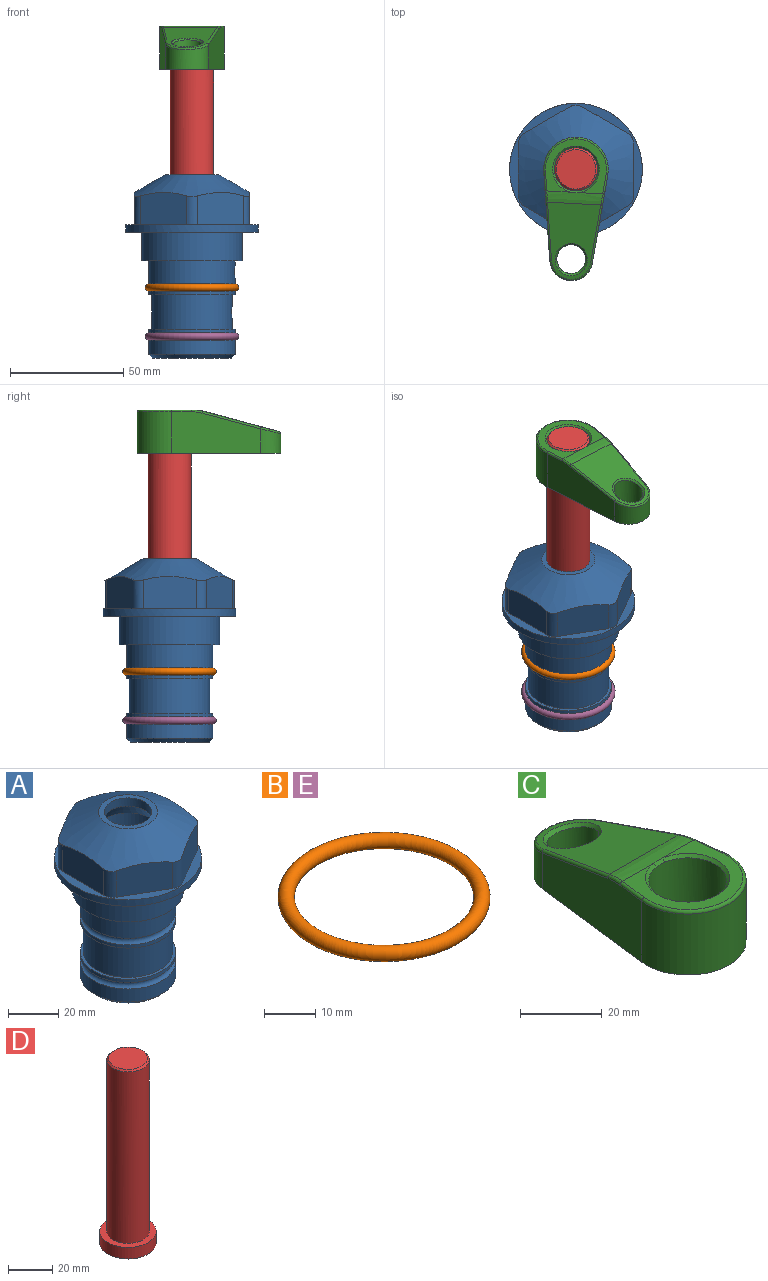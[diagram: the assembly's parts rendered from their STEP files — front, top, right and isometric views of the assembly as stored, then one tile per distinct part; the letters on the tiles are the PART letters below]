
ASSEMBLY  parts=5 mates=4
PART A: 36 faces, bbox 58.7x58.7x81 mm
  f0: cylinder r=17.78mm len=35.56mm, axis (0,0,1), area 1670.8mm2, adj f23,f24,f31
  f1: cylinder r=19.05mm len=38.1mm, axis (0,0,1), area 1191.9mm2, adj f26,f27,f30
  f2: plane 58.66x58.66mm, normal (0,0,-1), area 1150.6mm2, adj f3,f28
  f3: cylinder r=29.33mm len=58.66mm, axis (0,0,-1), area 585.1mm2, adj f2,f4
  f4: plane 58.66x58.66mm, normal (0,0,1), area 475.9mm2, adj f3,f5,f6,f7,f8,f9,f10,f11
  f5: plane 20.32x14.34mm, normal (-0.5,0.87,0), area 324.4mm2, adj f4,f15,f16,f17
  f6: plane 20.32x14.34mm, normal (0.5,0.87,0), area 324.4mm2, adj f4,f14,f15,f17
  f7: plane 23.48x14.34mm, normal (1,0,0), area 324.4mm2, adj f4,f13,f14,f17
  f8: plane 20.32x14.34mm, normal (0.5,-0.87,0), area 324.4mm2, adj f4,f12,f13,f17
  f9: plane 20.32x14.34mm, normal (-0.5,-0.87,0), area 324.4mm2, adj f4,f11,f12,f17
  f10: plane 23.48x14.34mm, normal (-1,0,0), area 324.4mm2, adj f4,f11,f16,f17
  f11: cylinder r=5.08mm len=12.85mm, axis (0,0,-1), area 67.2mm2, adj f4,f9,f10,f17
  f12: cylinder r=5.08mm len=12.85mm, axis (0,0,-1), area 67.2mm2, adj f4,f8,f9,f17
  f13: cylinder r=5.08mm len=12.85mm, axis (0,0,-1), area 67.2mm2, adj f4,f7,f8,f17
  f14: cylinder r=5.08mm len=12.85mm, axis (0,0,-1), area 67.2mm2, adj f4,f6,f7,f17
  f15: cylinder r=5.08mm len=12.85mm, axis (0,0,-1), area 67.2mm2, adj f4,f5,f6,f17
  f16: cylinder r=5.08mm len=12.85mm, axis (0,0,-1), area 67.2mm2, adj f4,f5,f10,f17
  f17: cone r=11.73mm half-angle=60deg, axis (0,0,-1), area 2071.8mm2, adj f5,f6,f7,f8,f9,f10,f11,f12
  f18: plane 23.46x23.46mm, normal (0,0,1), area 147.4mm2, adj f17,f35
  f19: plane 34.93x34.93mm, normal (0,0,-1), area 958mm2, adj f29
  f20: cylinder r=19.05mm len=38.1mm, axis (0,0,1), area 760.1mm2, adj f21,f29
  f21: torus R=19.05mm, axis (0,0,1), area 565.3mm2, adj f20,f22
  f22: cylinder r=19.05mm len=38.1mm, axis (0,0,1), area 190mm2, adj f21,f23
  f23: plane 38.1x38.1mm, normal (0,0,1), area 146.9mm2, adj f0,f22
  f24: plane 38.1x38.1mm, normal (0,0,-1), area 146.9mm2, adj f0,f25
  f25: cylinder r=19.05mm len=38.1mm, axis (0,0,1), area 190mm2, adj f24,f26
  f26: torus R=19.05mm, axis (0,0,1), area 565.3mm2, adj f1,f25
  f27: plane 44.45x44.45mm, normal (0,0,-1), area 411.7mm2, adj f1,f28
  f28: cylinder r=22.23mm len=44.45mm, axis (0,0,1), area 1773.5mm2, adj f2,f27
  f29: cone r=19.05mm half-angle=45deg, axis (0,0,1), area 257.5mm2, adj f19,f20
  f30: cylinder r=3.17mm len=6.75mm, axis (-1,0,0), area 128mm2, adj f1,f33
  f31: cylinder r=3.17mm len=6.35mm, axis (-1,0,0), area 102.5mm2, adj f0,f33
  f32: plane 25.4x25.4mm, normal (0,0,1), area 506.7mm2, adj f33
  f33: cylinder r=12.7mm len=66.42mm, axis (0,0,-1), area 5236.2mm2, adj f30,f31,f32,f34
  f34: cone r=9.53mm half-angle=30deg, axis (0,0,-1), area 443.4mm2, adj f33,f35
  f35: cylinder r=9.53mm len=19.05mm, axis (0,0,-1), area 240.9mm2, adj f18,f34
PART B: 1 faces, bbox 44.7x44.7x3.2 mm
  f0: torus R=19.05mm, axis (0,0,1), area 1193.9mm2
PART C: 31 faces, bbox 31.7x65.5x19.8 mm
  f0: plane 39.12x18.26mm, normal (0.99,0.12,0), area 612.2mm2, adj f1,f4,f7,f11,f13,f15
  f1: cylinder r=9.53mm len=18.91mm, axis (0,0,-1), area 296.1mm2, adj f0,f2,f7,f17
  f2: plane 39.12x18.26mm, normal (-0.99,0.12,0), area 612.2mm2, adj f1,f4,f7,f12,f14,f16
  f3: cylinder r=6.35mm len=12.7mm, axis (0,0,-1), area 362.4mm2, adj f7,f18
  f4: cylinder r=14.29mm len=28.58mm, axis (0,0,-1), area 882.2mm2, adj f0,f2,f7,f10
  f5: cylinder r=9.53mm len=19.05mm, axis (0,0,-1), area 1092.6mm2, adj f7,f19,f20
  f6: plane 26.99x23.69mm, normal (0,0,1), area 216.2mm2, adj f9,f10,f11,f12,f19
  f7: plane 63.5x28.58mm, normal (0,0,-1), area 661.8mm2, adj f0,f1,f2,f3,f4,f5,f22,f23
  f8: plane 33.52x23.6mm, normal (0,0.26,0.97), area 486mm2, adj f9,f15,f16,f17,f18
  f9: cylinder r=19.05mm len=24.72mm, axis (1,0,0), area 120.4mm2, adj f6,f8,f13,f14,f20
  f10: torus R=13.49mm, axis (0,0,1), area 59mm2, adj f4,f6,f11,f12
  f11: cylinder r=0.79mm len=8.67mm, axis (0.12,-0.99,0), area 10.8mm2, adj f0,f6,f10,f13
  f12: cylinder r=0.79mm len=8.67mm, axis (0.12,0.99,0), area 10.8mm2, adj f2,f6,f10,f14
  f13: bspline ~4.95x1.42mm, area 6.1mm2, adj f0,f9,f11,f15
  f14: bspline ~4.95x1.42mm, area 6.1mm2, adj f2,f9,f12,f16
  f15: cylinder r=0.79mm len=25.95mm, axis (0.12,-0.96,0.26), area 32.9mm2, adj f0,f8,f13,f17
  f16: cylinder r=0.79mm len=25.95mm, axis (0.12,0.96,-0.26), area 32.9mm2, adj f2,f8,f14,f17
  f17: bspline ~18.91x8.38mm, area 30mm2, adj f1,f8,f15,f16
  f18: bspline ~14.29x14.29mm, area 48.3mm2, adj f3,f8
  f19: cone r=9.53mm half-angle=45deg, axis (0,0,1), area 66.5mm2, adj f5,f6,f20
  f20: bspline ~3.22x0.96mm, area 3.5mm2, adj f5,f9,f19
  f21: plane 2.75x2.72mm, normal (0,0,-1), area 2.9mm2, adj f23,f25,f28
  f22: plane 23.05x15.88mm, normal (-0.99,-0.12,0), area 323.6mm2, adj f7,f25,f26,f27,f28,f29
  f23: plane 23.05x15.88mm, normal (0.99,-0.12,0), area 323.6mm2, adj f7,f21,f25,f27,f28,f30
  f24: cylinder r=9.53mm len=10.69mm, axis (0,0,-1), area 114.7mm2, adj f7,f27,f29,f30
  f25: cylinder r=12.7mm len=20.59mm, axis (0,0,-1), area 381.1mm2, adj f7,f21,f22,f23,f26,f28
  f26: plane 2.75x2.72mm, normal (0,0,-1), area 2.9mm2, adj f22,f25,f28
  f27: plane 19.72x18.37mm, normal (0,-0.26,-0.97), area 291.8mm2, adj f22,f23,f24,f28,f29,f30
  f28: cylinder r=15.88mm len=19.92mm, axis (1,0,0), area 54.8mm2, adj f21,f22,f23,f25,f26,f27
  f29: cylinder r=1.59mm len=11mm, axis (0,0,-1), area 34.7mm2, adj f7,f22,f24,f27
  f30: cylinder r=1.59mm len=11mm, axis (0,0,-1), area 34.7mm2, adj f7,f23,f24,f27
PART D: 6 faces, bbox 25.4x25.4x101.6 mm
  f0: plane 17.46x17.46mm, normal (0,0,1), area 239.5mm2, adj f5
  f1: plane 25.4x25.4mm, normal (0,0,-1), area 506.7mm2, adj f2
  f2: cylinder r=12.7mm len=25.4mm, axis (0,0,1), area 506.7mm2, adj f1,f3
  f3: plane 25.4x25.4mm, normal (0,0,1), area 221.7mm2, adj f2,f4
  f4: cylinder r=9.53mm len=94.46mm, axis (0,0,1), area 5653mm2, adj f3,f5
  f5: cone r=8.73mm half-angle=45deg, axis (0,0,-1), area 64.4mm2, adj f0,f4
PART E: same geometry as B
PLACE A at identity fixed
PLACE B at identity
PLACE C rot(axis=(0,0,1),177deg) t=(0,0,27.55)mm
PLACE D rot(axis=(0,0,1),177deg) t=(0,0,27.55)mm
PLACE E t=(0,0,-21.59)mm
MATE fastened A.f0 <-> E.f0  axis (0,0,1) through (0,0,-46.1)mm
MATE fastened D.f2 <-> C.f4  axis (0,0,-1) through (0,0,90.26)mm
MATE fastened A.f0 <-> B.f0  axis (0,0,1) through (0,0,-24.51)mm
MATE cylindrical A.f0 <-> D.f2  axis (0,0,1) through (0,0,-50.55)mm
